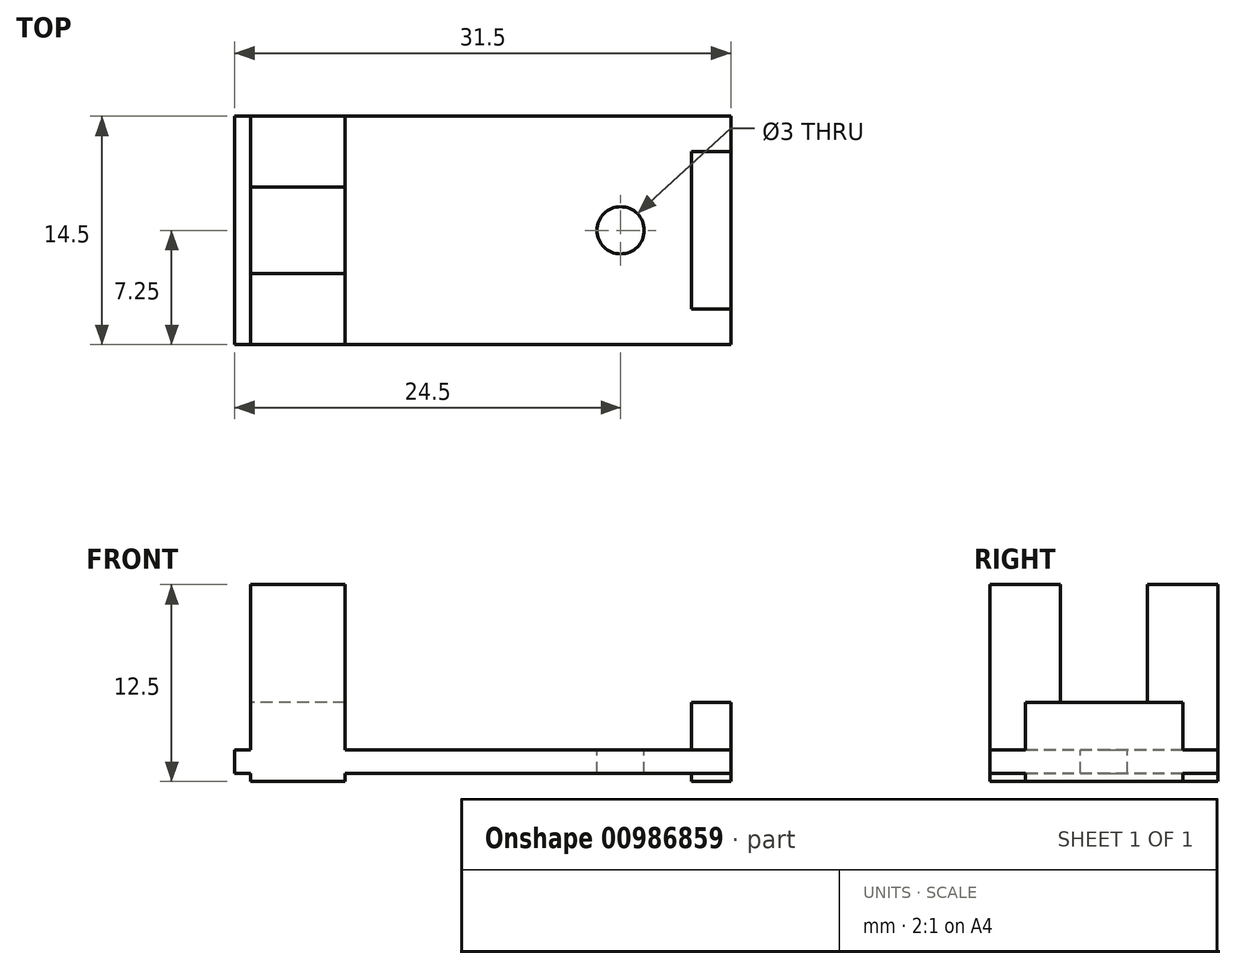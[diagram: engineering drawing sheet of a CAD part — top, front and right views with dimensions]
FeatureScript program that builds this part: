
annotation { "Feature Type Name" : "Feature", "Feature Type Description" : "" }
export const myFeature = defineFeature(function(context is Context, id is Id, definition is map)
    precondition{}
    {
        {
            var Q0;
            Q0=qCreatedBy(makeId("Top.planeOp"),FACE);
            var sketch = newSketch(context, id + "F0", { "sketchPlane" : qUnion([Q0])});
            skLineSegment(sketch, "E0.bottom", {"start": v(0, 0) * mm, "end": v(31.5, 0) * mm});
            skLineSegment(sketch, "E0.top", {"start": v(0, 14.5) * mm, "end": v(31.5, 14.5) * mm});
            skLineSegment(sketch, "E0.left", {"start": v(0, 0) * mm, "end": v(0, 14.5) * mm});
            skLineSegment(sketch, "E0.right", {"start": v(31.5, 0) * mm, "end": v(31.5, 14.5) * mm});
            skCircle(sketch, "E1", {"center": v(24.5, 7.25) * mm, "radius": 1.5 * mm});
            skLineSegment(sketch, "E2.bottom", {"start": v(31.5, 12.25) * mm, "end": v(29, 12.25) * mm});
            skLineSegment(sketch, "E2.top", {"start": v(31.5, 2.25) * mm, "end": v(29, 2.25) * mm});
            skLineSegment(sketch, "E2.left", {"start": v(31.5, 12.25) * mm, "end": v(31.5, 2.25) * mm});
            skLineSegment(sketch, "E2.right", {"start": v(29, 12.25) * mm, "end": v(29, 2.25) * mm});
            skLineSegment(sketch, "E3.bottom", {"start": v(1, 14.5) * mm, "end": v(7, 14.5) * mm});
            skLineSegment(sketch, "E3.top", {"start": v(1, 0) * mm, "end": v(7, 0) * mm});
            skLineSegment(sketch, "E3.left", {"start": v(1, 14.5) * mm, "end": v(1, 0) * mm});
            skLineSegment(sketch, "E3.right", {"start": v(7, 14.5) * mm, "end": v(7, 0) * mm});
            skLineSegment(sketch, "E4", {"start": v(1, 10) * mm, "end": v(7, 10) * mm});
            skLineSegment(sketch, "E5", {"start": v(1, 4.5) * mm, "end": v(7, 4.5) * mm});
            skSolve(sketch);
        }
        {
            var Q0;
            {var subQ3=sQuery(id+"F0.wireOp",EDGE,"E0.left");Q0=makeQuery(id+"F0.imprint","IMPRINT",FACE,{"disambiguationData":[TD([[makeQuery(id+"F0.imprint","IMPRINT",EDGE,{"derivedFrom":subQ3}),-1.0]])]});}
            var Q1;
            {var subQ5=sQuery(id+"F0.wireOp",EDGE,"E4");Q1=makeQuery(id+"F0.imprint","IMPRINT",FACE,{"disambiguationData":[TD([[makeQuery(id+"F0.imprint","IMPRINT",EDGE,{"derivedFrom":subQ5}),1.0]])]});}
            var Q2;
            {var subQ0=sQuery(id+"F0.wireOp",EDGE,"E4");Q2=makeQuery(id+"F0.imprint","IMPRINT",FACE,{"disambiguationData":[TD([[makeQuery(id+"F0.imprint","IMPRINT",EDGE,{"derivedFrom":subQ0}),-1.0]])]});}
            var Q3;
            {var subQ5=sQuery(id+"F0.wireOp",EDGE,"E5");Q3=makeQuery(id+"F0.imprint","IMPRINT",FACE,{"disambiguationData":[TD([[makeQuery(id+"F0.imprint","IMPRINT",EDGE,{"derivedFrom":subQ5}),-1.0]])]});}
            var Q4;
            Q4=makeQuery(id+"F0.imprint","IMPRINT",FACE,{"disambiguationData":[TD([[makeQuery(id+"F0.imprint","IMPRINT",EDGE,{"derivedFrom":sQuery(id+"F0.wireOp",EDGE,"E1")}),-1.0]])]});
            var Q5;
            {var subQ2=sQuery(id+"F0.wireOp",EDGE,"E2.bottom");Q5=makeQuery(id+"F0.imprint","IMPRINT",FACE,{"disambiguationData":[TD([[makeQuery(id+"F0.imprint","IMPRINT",EDGE,{"derivedFrom":subQ2}),1.0]])]});}
            extrude(context, id + "F1", {"entities" : qUnion([Q0, Q1, Q2, Q3, Q4, Q5]), "oppositeDirection" : true, "depth" : 1.5 * mm, "offsetDistance" : 25 * mm});
        }
        {
            var Q0;
            {var subQ2=sQuery(id+"F0.wireOp",EDGE,"E2.bottom");Q0=makeQuery(id+"F0.imprint","IMPRINT",FACE,{"disambiguationData":[TD([[makeQuery(id+"F0.imprint","IMPRINT",EDGE,{"derivedFrom":subQ2}),1.0]])]});}
            var Q1;
            {var subQ5=sQuery(id+"F0.wireOp",EDGE,"E4");Q1=makeQuery(id+"F0.imprint","IMPRINT",FACE,{"disambiguationData":[TD([[makeQuery(id+"F0.imprint","IMPRINT",EDGE,{"derivedFrom":subQ5}),1.0]])]});}
            var Q2;
            {var subQ0=sQuery(id+"F0.wireOp",EDGE,"E4");Q2=makeQuery(id+"F0.imprint","IMPRINT",FACE,{"disambiguationData":[TD([[makeQuery(id+"F0.imprint","IMPRINT",EDGE,{"derivedFrom":subQ0}),-1.0]])]});}
            var Q3;
            {var subQ5=sQuery(id+"F0.wireOp",EDGE,"E5");Q3=makeQuery(id+"F0.imprint","IMPRINT",FACE,{"disambiguationData":[TD([[makeQuery(id+"F0.imprint","IMPRINT",EDGE,{"derivedFrom":subQ5}),-1.0]])]});}
            extrude(context, id + "F2", {"entities" : qUnion([Q0, Q1, Q2, Q3]), "operationType" : NewBodyOperationType.ADD, "depth" : 3 * mm, "offsetDistance" : 25 * mm});
        }
        {
            var Q0;
            {var subQ5=sQuery(id+"F0.wireOp",EDGE,"E4");Q0=makeQuery(id+"F0.imprint","IMPRINT",FACE,{"disambiguationData":[TD([[makeQuery(id+"F0.imprint","IMPRINT",EDGE,{"derivedFrom":subQ5}),1.0]])]});}
            var Q1;
            {var subQ5=sQuery(id+"F0.wireOp",EDGE,"E5");Q1=makeQuery(id+"F0.imprint","IMPRINT",FACE,{"disambiguationData":[TD([[makeQuery(id+"F0.imprint","IMPRINT",EDGE,{"derivedFrom":subQ5}),-1.0]])]});}
            extrude(context, id + "F3", {"entities" : qUnion([Q0, Q1]), "operationType" : NewBodyOperationType.ADD, "depth" : 10.5 * mm, "offsetDistance" : 25 * mm});
        }
        {
            var Q0;
            {var subQ5=sQuery(id+"F0.wireOp",EDGE,"E4");Q0=makeQuery(id+"F0.imprint","IMPRINT",FACE,{"disambiguationData":[TD([[makeQuery(id+"F0.imprint","IMPRINT",EDGE,{"derivedFrom":subQ5}),1.0]])]});}
            var Q1;
            {var subQ0=sQuery(id+"F0.wireOp",EDGE,"E4");Q1=makeQuery(id+"F0.imprint","IMPRINT",FACE,{"disambiguationData":[TD([[makeQuery(id+"F0.imprint","IMPRINT",EDGE,{"derivedFrom":subQ0}),-1.0]])]});}
            var Q2;
            {var subQ5=sQuery(id+"F0.wireOp",EDGE,"E5");Q2=makeQuery(id+"F0.imprint","IMPRINT",FACE,{"disambiguationData":[TD([[makeQuery(id+"F0.imprint","IMPRINT",EDGE,{"derivedFrom":subQ5}),-1.0]])]});}
            var Q3;
            {var subQ2=sQuery(id+"F0.wireOp",EDGE,"E2.bottom");Q3=makeQuery(id+"F0.imprint","IMPRINT",FACE,{"disambiguationData":[TD([[makeQuery(id+"F0.imprint","IMPRINT",EDGE,{"derivedFrom":subQ2}),1.0]])]});}
            extrude(context, id + "F4", {"entities" : qUnion([Q0, Q1, Q2, Q3]), "operationType" : NewBodyOperationType.ADD, "oppositeDirection" : true, "depth" : 2 * mm, "offsetDistance" : 25 * mm});
        }
    });
